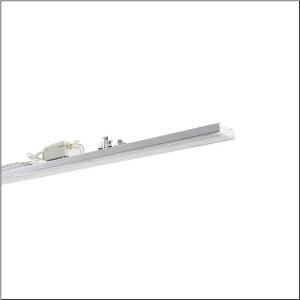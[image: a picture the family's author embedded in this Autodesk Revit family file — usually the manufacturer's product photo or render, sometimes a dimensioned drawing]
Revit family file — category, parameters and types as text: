
# Revit family: licross_r__21_recessed_mo_52tl1edn495g_86f5
name_source: partatom
category: Lighting Fixtures
units: mm (PartAtom-declared; Revit-internal decimal feet)

## family parameters
Cut with Voids When Loaded = No
Host = Face
Light Source = No
Part Type = Normal
Room Calculation Point = No
Round Connector Dimension = Use Diameter
Shared = No

## types (1)
- --- (1 x LED, 9940 lm, 58 W, 4000K)
    Apparent Load = 58 VA
    CIE Flux Codes = 85 95 99 100 100
    Color Rendering = 80
    Color Temperature = 4000K
    Default Elevation = 1800 mm
    Description = Licross® 21 Recessed MO, luminaire insert, of sheet steel, galvanised, coil coated, white, length: 1.500mm, width: 66mm, height: 67mm, LED rated luminous flux: 9.940lm, light colour: 840, control gear: DALI 2, with plug, 5-pole, with phase selection, mains connection: 220..240V, AC, 50/60Hz, rated input power: 58W, halogen-free wiring, primary light control with lens, of plastic, primary optical cover: cover, of PMMA, light emission: direct distribution, primary light characteristic: symmetric, protection rating (complete): IP40, insulation class (complete): insulation class I (protective earthing), certification: CE, ENEC, VDE, UKCA, protection symbol: D if used in an environment without relevant dust loads with corresponding accessories, impact resistance: IK06, permissible ambient temperature for indoor applications: -25..+35°C, corresponds to IFS (International Featured Standards) requirements for safety and quality in the food industry, reducing of maximum allowable ambient temperature of 5°C with ceiling mounting, LABS conformity tested according to VDMA 24364:2018-05, packaging unit: 1 piece
    Height = 58 mm
    Lamp = 1 x LED
    Lamp Light Flux = 9940 lm
    Lamp Power = 58 W
    Lamp count = 1
    Length = 1500 mm
    Luminous efficacy = 171 lm/W
    Manufacturer = Siteco
    ModVariant = No
    Model = 52TL1EDN495G
    Mounting Place = Ceiling
    Mounting Type = Pendant
    Number of Poles = 1
    OnlyDefault = Yes
    Power Factor = 1
    Product Name = Licross® 21 Recessed MO
    Product group = luminaire insert
    ProductGroupID = 901
    Protection Class = Protection class I
    Protection Degree = IP 40
    RLX_Detail_Level = 1
    RLX_Emergency_Light_Flux = 0 lm
    RLX_Emergency_Type = 0
    RLX_Emergency_Type_DB = No
    RlxData = <blob elided: 24709 chars, md5=dad1df2a>
    Socket = socket
    Standby Power = 0 W
    System Light Flux = 9940 lm
    System Power = 58 W
    Type Comments = factory setting: luminous flux: 100 % | dim-lin: 254 | 390 mA
    Type Image = l_1296930.jpg
    URL = http://relux.com
    VarID = @adj_056755
    Voltage = 0 V
    Weight = 0.00 kg
    Width = 66 mm

## geometry (parser evidence)
native form markers: Blend x4, Sweep x11
no freeform markers — native parametric forms only
